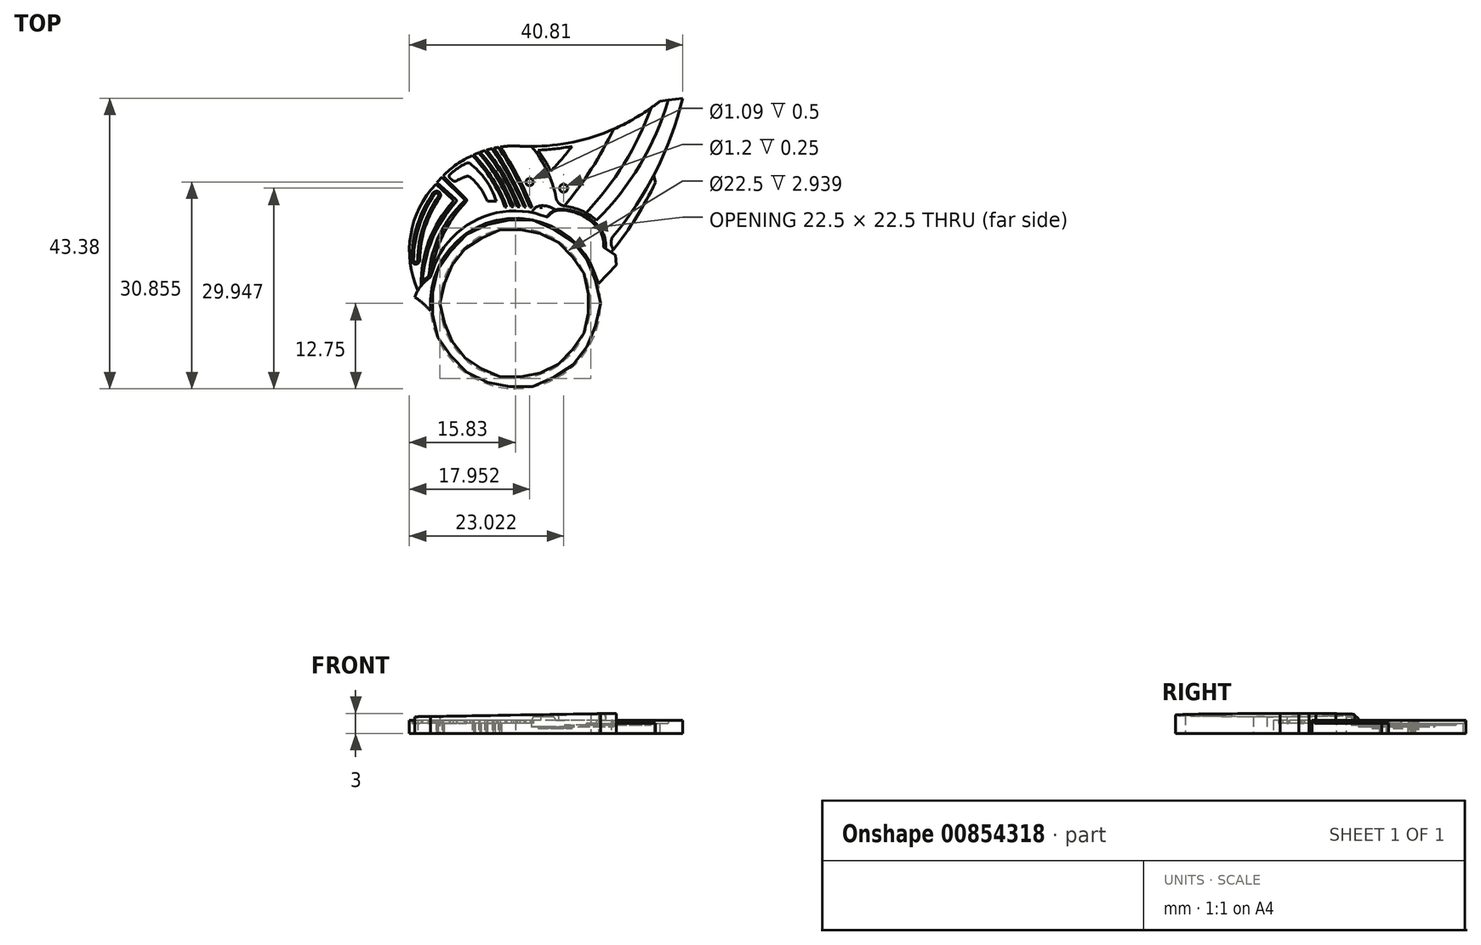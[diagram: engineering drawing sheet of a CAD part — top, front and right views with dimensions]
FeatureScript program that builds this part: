
annotation { "Feature Type Name" : "Feature", "Feature Type Description" : "" }
export const myFeature = defineFeature(function(context is Context, id is Id, definition is map)
    precondition{}
    {
        {
            var Q0;
            Q0=qCreatedBy(makeId("Top.planeOp"),FACE);
            var sketch = newSketch(context, id + "F0", { "sketchPlane" : qUnion([Q0])});
            skCircle(sketch, "E0", {"center": v(0, 0) * mm, "radius": 11.25 * mm});
            skCircle(sketch, "E1", {"center": v(0, 0) * mm, "radius": 12.75 * mm});
            skCircle(sketch, "E2", {"center": v(0, 0) * mm, "radius": 10.25 * mm});
            skSolve(sketch);
        }
        {
            var Q0;
            Q0=makeQuery(id+"F0.imprint","IMPRINT",FACE,{"disambiguationData":[TD([[makeQuery(id+"F0.imprint","IMPRINT",EDGE,{"derivedFrom":sQuery(id+"F0.wireOp",EDGE,"E0")}),-1.0]])]});
            var Q1;
            Q1=makeQuery(id+"F0.imprint","IMPRINT",FACE,{"disambiguationData":[TD([[makeQuery(id+"F0.imprint","IMPRINT",EDGE,{"derivedFrom":sQuery(id+"F0.wireOp",EDGE,"E0")}),1.0]])]});
            extrude(context, id + "F1", {"entities" : qUnion([Q0, Q1]), "endBound" : BoundingType.SYMMETRIC, "oppositeDirection" : true, "depth" : 9 * mm, "offsetDistance" : 25 * mm});
        }
        {
            var Q0;
            Q0=makeQuery(id+"F0.imprint","IMPRINT",FACE,{"disambiguationData":[TD([[makeQuery(id+"F0.imprint","IMPRINT",EDGE,{"derivedFrom":sQuery(id+"F0.wireOp",EDGE,"E0")}),1.0]])]});
            extrude(context, id + "F2", {"entities" : qUnion([Q0]), "operationType" : NewBodyOperationType.REMOVE, "depth" : 3.5 * mm, "offsetDistance" : 25 * mm});
        }
        {
            var Q0;
            Q0=qCreatedBy(makeId("Top.planeOp"),FACE);
            var sketch = newSketch(context, id + "F3", { "sketchPlane" : qUnion([Q0])});
            skCircle(sketch, "E3", {"center": v(0, 0) * mm, "radius": 10.25 * mm});
            skArc(sketch, "E4", {"start": v(-2, 8) * mm, "mid": v(-8.25, 0) * mm, "end": v(-2, -8) * mm});
            skLineSegment(sketch, "E5.left", {"start": v(-2, 8) * mm, "end": v(-2, -8) * mm});
            skLineSegment(sketch, "E5.right", {"start": v(2, 8) * mm, "end": v(2, -8) * mm});
            skLineSegment(sketch, "E6", {"start": v(-2, 8) * mm, "end": v(2, -8) * mm, "construction": true});
            skArc(sketch, "E7.trimOffspring", {"start": v(2, -8) * mm, "mid": v(8.25, 0) * mm, "end": v(2, 8) * mm});
            skSolve(sketch);
        }
        {
            var Q0;
            Q0=makeQuery(id+"F3.imprint","IMPRINT",FACE,{"disambiguationData":[TD([[makeQuery(id+"F3.imprint","IMPRINT",EDGE,{"derivedFrom":sQuery(id+"F3.wireOp",EDGE,"E3")}),1.0]])]});
            extrude(context, id + "F4", {"entities" : qUnion([Q0]), "oppositeDirection" : true, "depth" : 2 * mm, "offsetDistance" : 25 * mm});
        }
        {
            var Q0;
            Q0=makeQuery(id+"F4.opExtrude","SWEPT_BODY",BODY,{"disambiguationData":[OSD([sQuery(id+"F3.wireOp",EDGE,"E3"),sQuery(id+"F3.wireOp",EDGE,"E4"),sQuery(id+"F3.wireOp",EDGE,"E5.left"),sQuery(id+"F3.wireOp",EDGE,"E5.right"),sQuery(id+"F3.wireOp",EDGE,"E7.trimOffspring")])]});
            deleteBodies(context, id + "F5", {"entities" : qUnion([Q0])});
        }
        {
            var Q0;
            Q0=makeQuery(id+"F0.imprint","IMPRINT",FACE,{"disambiguationData":[TD([[makeQuery(id+"F0.imprint","IMPRINT",EDGE,{"derivedFrom":sQuery(id+"F0.wireOp",EDGE,"E0")}),1.0]])]});
            extrude(context, id + "F6", {"entities" : qUnion([Q0]), "operationType" : NewBodyOperationType.REMOVE, "oppositeDirection" : true, "depth" : 3.5 * mm, "offsetDistance" : 25 * mm});
        }
        {
            var Q0;
            Q0=qCreatedBy(makeId("Top.planeOp"),FACE);
            var sketch = newSketch(context, id + "F7", { "sketchPlane" : qUnion([Q0])});
            skCircle(sketch, "E8.cCircle", {"center": v(0, 0) * mm, "radius": 12.75 * mm});
            skLineSegment(sketch, "E8.0", {"start": v(-12.75, 0) * mm, "end": v(6.38, 11.04) * mm, "construction": true});
            skLineSegment(sketch, "E8.1", {"start": v(6.37, 11.04) * mm, "end": v(6.38, -11.04) * mm, "construction": true});
            skLineSegment(sketch, "E8.2", {"start": v(6.38, -11.04) * mm, "end": v(-12.75, 0) * mm, "construction": true});
            skCircle(sketch, "E9.0", {"center": v(0, 0) * mm, "radius": 12.75 * mm, "construction": true});
            skArc(sketch, "E10", {"start": v(0, 23.52) * mm, "mid": v(-1.13, 23.48) * mm, "end": v(-2.26, 23.35) * mm});
            skArc(sketch, "E11", {"start": v(0, 23.52) * mm, "mid": v(11.42, 24.82) * mm, "end": v(21.58, 30.2) * mm});
            skLineSegment(sketch, "E12", {"start": v(21.58, 30.2) * mm, "end": v(24.98, 30.63) * mm});
            skArc(sketch, "E13", {"start": v(14.56, 10) * mm, "mid": v(20.98, 19.7) * mm, "end": v(24.98, 30.63) * mm});
            skLineSegment(sketch, "E14", {"start": v(20.67, 19.1) * mm, "end": v(20.94, 18.08) * mm});
            skArc(sketch, "E15", {"start": v(14.3, 7.63) * mm, "mid": v(17.93, 12.66) * mm, "end": v(20.94, 18.08) * mm});
            skArc(sketch, "E16", {"start": v(12.1, 12.4) * mm, "mid": v(18.62, 20.7) * mm, "end": v(22.83, 30.36) * mm});
            skArc(sketch, "E17", {"start": v(10.53, 13.5) * mm, "mid": v(16.23, 20.84) * mm, "end": v(20.26, 29.2) * mm});
            skArc(sketch, "E18", {"start": v(7.32, 14.55) * mm, "mid": v(11.36, 20.06) * mm, "end": v(14.68, 26.03) * mm});
            skArc(sketch, "E19", {"start": v(6.08, 15.72) * mm, "mid": v(4.73, 19.82) * mm, "end": v(2.38, 23.43) * mm});
            skArc(sketch, "E20", {"start": v(12.1, 12.4) * mm, "mid": v(9.87, 13.84) * mm, "end": v(7.32, 14.55) * mm});
            skArc(sketch, "E21", {"start": v(6.08, 15.72) * mm, "mid": v(6.51, 14.94) * mm, "end": v(7.32, 14.55) * mm});
            skArc(sketch, "E22", {"start": v(5.26, 19.75) * mm, "mid": v(4.42, 21.36) * mm, "end": v(3.4, 22.88) * mm});
            skArc(sketch, "E23", {"start": v(3.4, 22.88) * mm, "mid": v(5.94, 23.07) * mm, "end": v(8.44, 23.46) * mm});
            skArc(sketch, "E24", {"start": v(5.26, 19.75) * mm, "mid": v(6.92, 21.55) * mm, "end": v(8.44, 23.46) * mm});
            skArc(sketch, "E25", {"start": v(2.48, 14.32) * mm, "mid": v(0.36, 18.97) * mm, "end": v(-2.26, 23.35) * mm});
            skArc(sketch, "E26", {"start": v(2.17, 14.35) * mm, "mid": v(0.05, 18.95) * mm, "end": v(-2.56, 23.3) * mm});
            skLineSegment(sketch, "E27", {"start": v(2.48, 14.32) * mm, "end": v(2.17, 14.35) * mm});
            skArc(sketch, "E28", {"start": v(-2.85, 15.27) * mm, "mid": v(-4.42, 18.41) * mm, "end": v(-6.85, 20.94) * mm});
            skArc(sketch, "E29", {"start": v(-7.36, 20.9) * mm, "mid": v(-8.63, 20.16) * mm, "end": v(-9.78, 19.23) * mm});
            skArc(sketch, "E30", {"start": v(-7.32, 18.95) * mm, "mid": v(-8.06, 18.68) * mm, "end": v(-8.75, 18.32) * mm});
            skArc(sketch, "E31", {"start": v(-4.18, 15.24) * mm, "mid": v(-5.24, 17.21) * mm, "end": v(-6.78, 18.84) * mm});
            skArc(sketch, "E32", {"start": v(-6.78, 18.84) * mm, "mid": v(-7.04, 18.97) * mm, "end": v(-7.32, 18.95) * mm});
            skArc(sketch, "E33", {"start": v(-6.85, 20.94) * mm, "mid": v(-7.1, 20.98) * mm, "end": v(-7.36, 20.9) * mm});
            skLineSegment(sketch, "E34", {"start": v(-9.8, 18.74) * mm, "end": v(-9.36, 18.33) * mm});
            skLineSegment(sketch, "E35", {"start": v(-4.18, 15.24) * mm, "end": v(-2.85, 15.27) * mm});
            skArc(sketch, "E36", {"start": v(-9.78, 19.23) * mm, "mid": v(-9.9, 19) * mm, "end": v(-9.8, 18.74) * mm});
            skArc(sketch, "E37", {"start": v(-9.36, 18.33) * mm, "mid": v(-9.06, 18.21) * mm, "end": v(-8.75, 18.32) * mm});
            skCircle(sketch, "E38", {"center": v(7.2, 17.2) * mm, "radius": 0.6 * mm});
            skCircle(sketch, "E39", {"center": v(2.12, 18.1) * mm, "radius": 0.55 * mm});
            skLineSegment(sketch, "E40", {"start": v(-10.8, 19.02) * mm, "end": v(-7.38, 15.63) * mm});
            skLineSegment(sketch, "E41", {"start": v(-10.8, 19.02) * mm, "end": v(-6.53, 23.33) * mm, "construction": true});
            skLineSegment(sketch, "E42", {"start": v(-10.98, 18.83) * mm, "end": v(-7.67, 15.55) * mm});
            skArc(sketch, "E43", {"start": v(-12.7, -1.1) * mm, "mid": v(-13.79, 0) * mm, "end": v(-15.02, 0.93) * mm});
            skArc(sketch, "E44", {"start": v(-12.67, 3.93) * mm, "mid": v(-14.09, 2.62) * mm, "end": v(-15.02, 0.93) * mm});
            skArc(sketch, "E45", {"start": v(4.7, 12.9) * mm, "mid": v(-6.04, 12.38) * mm, "end": v(-12.67, 3.93) * mm});
            skArc(sketch, "E46", {"start": v(14.56, 10) * mm, "mid": v(14.31, 9) * mm, "end": v(14.6, 8) * mm});
            skArc(sketch, "E47", {"start": v(12.67, 11.21) * mm, "mid": v(9.9, 13.36) * mm, "end": v(6.47, 14.07) * mm});
            skArc(sketch, "E48", {"start": v(13.44, 8.22) * mm, "mid": v(13.34, 9.8) * mm, "end": v(12.67, 11.21) * mm});
            skArc(sketch, "E49", {"start": v(6.47, 14.07) * mm, "mid": v(5.47, 13.66) * mm, "end": v(4.7, 12.9) * mm});
            skLineSegment(sketch, "E50", {"start": v(13.44, 8.22) * mm, "end": v(14.92, 7.21) * mm});
            skLineSegment(sketch, "E51", {"start": v(14.92, 7.21) * mm, "end": v(15.05, 5.7) * mm});
            skLineSegment(sketch, "E52", {"start": v(15.05, 5.7) * mm, "end": v(12.41, 2.9) * mm});
            skArc(sketch, "E53", {"start": v(-7.63, 15.26) * mm, "mid": v(-11.33, 10.22) * mm, "end": v(-12.9, 4.17) * mm});
            skArc(sketch, "E54", {"start": v(-7.34, 15.17) * mm, "mid": v(-10.84, 10.16) * mm, "end": v(-12.58, 4.3) * mm});
            skArc(sketch, "E55", {"start": v(-13.08, 3.93) * mm, "mid": v(-13.5, 3.62) * mm, "end": v(-13.86, 3.26) * mm});
            skArc(sketch, "E56", {"start": v(-8.9, 15.08) * mm, "mid": v(-12.4, 9.6) * mm, "end": v(-13.86, 3.26) * mm});
            skArc(sketch, "E57", {"start": v(-11.88, 17.81) * mm, "mid": v(-15.62, 10.26) * mm, "end": v(-14.58, 1.89) * mm});
            skLineSegment(sketch, "E58", {"start": v(-11.88, 17.81) * mm, "end": v(-9.33, 15.47) * mm});
            skLineSegment(sketch, "E59", {"start": v(-8.93, 15.6) * mm, "end": v(-11.7, 18.04) * mm});
            skArc(sketch, "E60", {"start": v(-9.38, 15.14) * mm, "mid": v(-12.9, 9.32) * mm, "end": v(-14.09, 2.62) * mm});
            skArc(sketch, "E61", {"start": v(-13.08, 3.93) * mm, "mid": v(-12.96, 4.03) * mm, "end": v(-12.9, 4.17) * mm});
            skArc(sketch, "E62", {"start": v(-9.38, 15.14) * mm, "mid": v(-9.3, 15.3) * mm, "end": v(-9.33, 15.47) * mm});
            skArc(sketch, "E63", {"start": v(-8.9, 15.08) * mm, "mid": v(-8.8, 15.34) * mm, "end": v(-8.93, 15.6) * mm});
            skArc(sketch, "E64", {"start": v(-7.63, 15.26) * mm, "mid": v(-7.6, 15.41) * mm, "end": v(-7.67, 15.55) * mm});
            skArc(sketch, "E65", {"start": v(-7.34, 15.17) * mm, "mid": v(-7.28, 15.4) * mm, "end": v(-7.38, 15.63) * mm});
            skArc(sketch, "E66", {"start": v(-11.5, 16) * mm, "mid": v(-13.77, 11.46) * mm, "end": v(-14.58, 6.46) * mm});
            skArc(sketch, "E67", {"start": v(-12.02, 16.34) * mm, "mid": v(-14.35, 11.64) * mm, "end": v(-15.2, 6.47) * mm});
            skArc(sketch, "E68", {"start": v(-15.2, 6.47) * mm, "mid": v(-14.9, 6.15) * mm, "end": v(-14.58, 6.46) * mm});
            skArc(sketch, "E69", {"start": v(-11.5, 16) * mm, "mid": v(-11.6, 16.4) * mm, "end": v(-12.02, 16.34) * mm});
            skArc(sketch, "E70.0", {"start": v(-11.24, 15.83) * mm, "mid": v(-13.48, 11.38) * mm, "end": v(-14.28, 6.46) * mm});
            skArc(sketch, "E70.1", {"start": v(-11.24, 15.83) * mm, "mid": v(-11.43, 16.66) * mm, "end": v(-12.27, 16.51) * mm});
            skArc(sketch, "E70.2", {"start": v(-12.27, 16.51) * mm, "mid": v(-14.63, 11.74) * mm, "end": v(-15.5, 6.48) * mm});
            skArc(sketch, "E70.3", {"start": v(-15.5, 6.48) * mm, "mid": v(-14.9, 5.85) * mm, "end": v(-14.28, 6.46) * mm});
            skArc(sketch, "E71", {"start": v(5.99, 13.93) * mm, "mid": v(4.96, 14.45) * mm, "end": v(3.82, 14.58) * mm});
            skArc(sketch, "E72", {"start": v(3.82, 14.58) * mm, "mid": v(3, 14.28) * mm, "end": v(2.47, 13.57) * mm});
            skLineSegment(sketch, "E73", {"start": v(-11.76, 17.7) * mm, "end": v(-11.56, 17.92) * mm});
            skLineSegment(sketch, "E74", {"start": v(-10.84, 18.69) * mm, "end": v(-10.66, 18.87) * mm});
            skLineSegment(sketch, "E75", {"start": v(-2.4, 23.05) * mm, "end": v(-2.1, 23.1) * mm});
            skArc(sketch, "E76", {"start": v(2.17, 14.35) * mm, "mid": v(0.32, 14.41) * mm, "end": v(-1.53, 14.35) * mm});
            skArc(sketch, "E77", {"start": v(-1.53, 14.35) * mm, "mid": v(-3.6, 18.46) * mm, "end": v(-6.43, 22.1) * mm});
            skArc(sketch, "E78", {"start": v(-1.28, 14.36) * mm, "mid": v(-3.34, 18.53) * mm, "end": v(-6.19, 22.2) * mm});
            skArc(sketch, "E79", {"start": v(1.53, 14.38) * mm, "mid": v(-0.62, 18.9) * mm, "end": v(-3.2, 23.18) * mm});
            skArc(sketch, "E80", {"start": v(1.28, 14.4) * mm, "mid": v(-0.9, 18.87) * mm, "end": v(-3.5, 23.11) * mm});
            skArc(sketch, "E81", {"start": v(0.64, 14.41) * mm, "mid": v(-1.5, 18.85) * mm, "end": v(-4.3, 22.9) * mm});
            skArc(sketch, "E82", {"start": v(0.26, 14.41) * mm, "mid": v(-1.79, 18.83) * mm, "end": v(-4.6, 22.8) * mm});
            skArc(sketch, "E83", {"start": v(-0.3, 14.4) * mm, "mid": v(-2.38, 18.74) * mm, "end": v(-5.28, 22.57) * mm});
            skArc(sketch, "E84", {"start": v(-0.62, 14.4) * mm, "mid": v(-2.7, 18.66) * mm, "end": v(-5.5, 22.5) * mm});
            skArc(sketch, "E85", {"start": v(-3.04, 22.95) * mm, "mid": v(-3.2, 22.92) * mm, "end": v(-3.34, 22.89) * mm});
            skArc(sketch, "E86.trimOffspring", {"start": v(-4.14, 22.7) * mm, "mid": v(-4.28, 22.65) * mm, "end": v(-4.43, 22.61) * mm});
            skArc(sketch, "E87.trimOffspring", {"start": v(-5.1, 22.39) * mm, "mid": v(-5.22, 22.35) * mm, "end": v(-5.34, 22.3) * mm});
            skArc(sketch, "E88.trimOffspring", {"start": v(-6.02, 22.03) * mm, "mid": v(-6.14, 21.97) * mm, "end": v(-6.26, 21.92) * mm});
            skArc(sketch, "E89.trimOffspring", {"start": v(-6.43, 22.1) * mm, "mid": v(-8.75, 20.75) * mm, "end": v(-10.8, 19.02) * mm});
            skArc(sketch, "E90.trimOffspring", {"start": v(-5.5, 22.5) * mm, "mid": v(-5.85, 22.35) * mm, "end": v(-6.19, 22.2) * mm});
            skArc(sketch, "E91.trimOffspring", {"start": v(-4.6, 22.8) * mm, "mid": v(-4.94, 22.7) * mm, "end": v(-5.28, 22.57) * mm});
            skArc(sketch, "E92.trimOffspring", {"start": v(-3.5, 23.11) * mm, "mid": v(-3.9, 23.01) * mm, "end": v(-4.3, 22.9) * mm});
            skArc(sketch, "E93.trimOffspring", {"start": v(-2.56, 23.3) * mm, "mid": v(-2.88, 23.24) * mm, "end": v(-3.2, 23.18) * mm});
            skArc(sketch, "E94.trimOffspring", {"start": v(-10.98, 18.83) * mm, "mid": v(-11.35, 18.44) * mm, "end": v(-11.7, 18.04) * mm});
            skSolve(sketch);
        }
        {
            var Q0;
            {var subQ8=sQuery(id+"F7.wireOp",EDGE,"E43");Q0=makeQuery(id+"F7.imprint","IMPRINT",FACE,{"disambiguationData":[TD([[makeQuery(id+"F7.imprint","IMPRINT",EDGE,{"derivedFrom":subQ8}),-1.0]])]});}
            extrude(context, id + "F8", {"entities" : qUnion([Q0]), "endBound" : BoundingType.SYMMETRIC, "depth" : 6 * mm, "offsetDistance" : 25 * mm});
        }
        {
            var Q0;
            {var subQ9=sQuery(id+"F7.wireOp",EDGE,"E16");Q0=makeQuery(id+"F7.imprint","IMPRINT",FACE,{"disambiguationData":[TD([[makeQuery(id+"F7.imprint","IMPRINT",EDGE,{"derivedFrom":subQ9}),-1.0]])]});}
            var Q1;
            {var subQ1=sQuery(id+"F7.wireOp",EDGE,"E57");Q1=makeQuery(id+"F7.imprint","IMPRINT",FACE,{"disambiguationData":[TD([[makeQuery(id+"F7.imprint","IMPRINT",EDGE,{"derivedFrom":subQ1}),1.0]])]});}
            var Q2;
            Q2=makeQuery(id+"F7.imprint","IMPRINT",FACE,{"disambiguationData":[TD([[makeQuery(id+"F7.imprint","IMPRINT",EDGE,{"derivedFrom":sQuery(id+"F7.wireOp",EDGE,"E66")}),-1.0]])]});
            var Q3;
            {var subQ0=sQuery(id+"F7.wireOp",EDGE,"E42");Q3=makeQuery(id+"F7.imprint","IMPRINT",FACE,{"disambiguationData":[TD([[makeQuery(id+"F7.imprint","IMPRINT",EDGE,{"derivedFrom":subQ0}),-1.0]])]});}
            var Q4;
            {var subQ5=sQuery(id+"F7.wireOp",EDGE,"E93.trimOffspring");Q4=makeQuery(id+"F7.imprint","IMPRINT",FACE,{"disambiguationData":[TD([[makeQuery(id+"F7.imprint","IMPRINT",EDGE,{"derivedFrom":subQ5}),1.0]])]});}
            var Q5;
            {var subQ4=sQuery(id+"F7.wireOp",EDGE,"E92.trimOffspring");Q5=makeQuery(id+"F7.imprint","IMPRINT",FACE,{"disambiguationData":[TD([[makeQuery(id+"F7.imprint","IMPRINT",EDGE,{"derivedFrom":subQ4}),1.0]])]});}
            var Q6;
            {var subQ7=sQuery(id+"F7.wireOp",EDGE,"E91.trimOffspring");Q6=makeQuery(id+"F7.imprint","IMPRINT",FACE,{"disambiguationData":[TD([[makeQuery(id+"F7.imprint","IMPRINT",EDGE,{"derivedFrom":subQ7}),1.0]])]});}
            var Q7;
            {var subQ4=sQuery(id+"F7.wireOp",EDGE,"E90.trimOffspring");Q7=makeQuery(id+"F7.imprint","IMPRINT",FACE,{"disambiguationData":[TD([[makeQuery(id+"F7.imprint","IMPRINT",EDGE,{"derivedFrom":subQ4}),1.0]])]});}
            extrude(context, id + "F9", {"entities" : qUnion([Q0, Q1, Q2, Q3, Q4, Q5, Q6, Q7]), "operationType" : NewBodyOperationType.ADD, "endBound" : BoundingType.SYMMETRIC, "depth" : 4 * mm, "offsetDistance" : 25 * mm});
        }
        {
            var Q0;
            {var subQ4=sQuery(id+"F7.wireOp",EDGE,"E71");Q0=makeQuery(id+"F7.imprint","IMPRINT",FACE,{"disambiguationData":[TD([[makeQuery(id+"F7.imprint","IMPRINT",EDGE,{"derivedFrom":subQ4}),1.0]])]});}
            extrude(context, id + "F10", {"entities" : qUnion([Q0]), "operationType" : NewBodyOperationType.ADD, "endBound" : BoundingType.SYMMETRIC, "depth" : 5 * mm, "offsetDistance" : 25 * mm});
        }
        {
            var Q0;
            Q0=makeQuery(id+"F7.imprint","IMPRINT",FACE,{"disambiguationData":[TD([[makeQuery(id+"F7.imprint","IMPRINT",EDGE,{"derivedFrom":sQuery(id+"F7.wireOp",EDGE,"E28")}),1.0]])]});
            var Q1;
            {var subQ5=sQuery(id+"F7.wireOp",EDGE,"E40");Q1=makeQuery(id+"F7.imprint","IMPRINT",FACE,{"disambiguationData":[TD([[makeQuery(id+"F7.imprint","IMPRINT",EDGE,{"derivedFrom":subQ5}),-1.0]])]});}
            var Q2;
            Q2=makeQuery(id+"F7.imprint","IMPRINT",FACE,{"disambiguationData":[TD([[makeQuery(id+"F7.imprint","IMPRINT",EDGE,{"derivedFrom":sQuery(id+"F7.wireOp",EDGE,"E66")}),1.0]])]});
            var Q3;
            Q3=makeQuery(id+"F7.imprint","IMPRINT",FACE,{"disambiguationData":[TD([[makeQuery(id+"F7.imprint","IMPRINT",EDGE,{"derivedFrom":sQuery(id+"F7.wireOp",EDGE,"E39")}),1.0]])]});
            var Q4;
            {var subQ2=sQuery(id+"F7.wireOp",EDGE,"E14");Q4=makeQuery(id+"F7.imprint","IMPRINT",FACE,{"disambiguationData":[TD([[makeQuery(id+"F7.imprint","IMPRINT",EDGE,{"derivedFrom":subQ2}),-1.0]])]});}
            var Q5;
            {var subQ5=sQuery(id+"F7.wireOp",EDGE,"E88.trimOffspring");Q5=makeQuery(id+"F7.imprint","IMPRINT",FACE,{"disambiguationData":[TD([[makeQuery(id+"F7.imprint","IMPRINT",EDGE,{"derivedFrom":subQ5}),1.0]])]});}
            var Q6;
            {var subQ5=sQuery(id+"F7.wireOp",EDGE,"E87.trimOffspring");Q6=makeQuery(id+"F7.imprint","IMPRINT",FACE,{"disambiguationData":[TD([[makeQuery(id+"F7.imprint","IMPRINT",EDGE,{"derivedFrom":subQ5}),1.0]])]});}
            var Q7;
            {var subQ5=sQuery(id+"F7.wireOp",EDGE,"E86.trimOffspring");Q7=makeQuery(id+"F7.imprint","IMPRINT",FACE,{"disambiguationData":[TD([[makeQuery(id+"F7.imprint","IMPRINT",EDGE,{"derivedFrom":subQ5}),1.0]])]});}
            var Q8;
            {var subQ5=sQuery(id+"F7.wireOp",EDGE,"E85");Q8=makeQuery(id+"F7.imprint","IMPRINT",FACE,{"disambiguationData":[TD([[makeQuery(id+"F7.imprint","IMPRINT",EDGE,{"derivedFrom":subQ5}),1.0]])]});}
            var Q9;
            {var subQ0=sQuery(id+"F7.wireOp",EDGE,"E27");Q9=makeQuery(id+"F7.imprint","IMPRINT",FACE,{"disambiguationData":[TD([[makeQuery(id+"F7.imprint","IMPRINT",EDGE,{"derivedFrom":subQ0}),-1.0]])]});}
            var Q10;
            {var subQ1=sQuery(id+"F7.wireOp",EDGE,"E16");Q10=makeQuery(id+"F7.imprint","IMPRINT",FACE,{"disambiguationData":[TD([[makeQuery(id+"F7.imprint","IMPRINT",EDGE,{"derivedFrom":subQ1}),1.0]])]});}
            extrude(context, id + "F11", {"entities" : qUnion([Q0, Q1, Q2, Q3, Q4, Q5, Q6, Q7, Q8, Q9, Q10]), "operationType" : NewBodyOperationType.ADD, "endBound" : BoundingType.SYMMETRIC, "depth" : 3 * mm, "offsetDistance" : 25 * mm});
        }
        {
            var Q0;
            {var subQ0=sQuery(id+"F7.wireOp",EDGE,"E17");Q0=makeQuery(id+"F7.imprint","IMPRINT",FACE,{"disambiguationData":[TD([[makeQuery(id+"F7.imprint","IMPRINT",EDGE,{"derivedFrom":subQ0}),1.0]])]});}
            extrude(context, id + "F12", {"entities" : qUnion([Q0]), "operationType" : NewBodyOperationType.ADD, "endBound" : BoundingType.SYMMETRIC, "depth" : 2.5 * mm, "offsetDistance" : 25 * mm});
        }
        {
            var Q0;
            {var subQ1=sQuery(id+"F7.wireOp",EDGE,"E18");Q0=makeQuery(id+"F7.imprint","IMPRINT",FACE,{"disambiguationData":[TD([[makeQuery(id+"F7.imprint","IMPRINT",EDGE,{"derivedFrom":subQ1}),1.0]])]});}
            extrude(context, id + "F13", {"entities" : qUnion([Q0]), "operationType" : NewBodyOperationType.ADD, "endBound" : BoundingType.SYMMETRIC, "depth" : 2 * mm, "offsetDistance" : 25 * mm});
        }
        {
            var Q0;
            Q0=makeQuery(id+"F7.imprint","IMPRINT",FACE,{"disambiguationData":[TD([[makeQuery(id+"F7.imprint","IMPRINT",EDGE,{"derivedFrom":sQuery(id+"F7.wireOp",EDGE,"E38")}),1.0]])]});
            var Q1;
            Q1=makeQuery(id+"F7.imprint","IMPRINT",FACE,{"disambiguationData":[TD([[makeQuery(id+"F7.imprint","IMPRINT",EDGE,{"derivedFrom":sQuery(id+"F7.wireOp",EDGE,"E22")}),-1.0]])]});
            extrude(context, id + "F14", {"entities" : qUnion([Q0, Q1]), "operationType" : NewBodyOperationType.ADD, "endBound" : BoundingType.SYMMETRIC, "depth" : 1.5 * mm, "offsetDistance" : 25 * mm});
        }
        {
            var Q0;
            Q0=makeQuery(id+"F8.opExtrude","CAP_EDGE",EDGE,{"disambiguationData":[OSD([sQuery(id+"F7.wireOp",EDGE,"E49")])],"isStart":false});
            var Q1;
            Q1=makeQuery(id+"F8.opExtrude","CAP_EDGE",EDGE,{"disambiguationData":[OSD([sQuery(id+"F7.wireOp",EDGE,"E47")])],"isStart":false});
            var Q2;
            Q2=makeQuery(id+"F8.opExtrude","CAP_EDGE",EDGE,{"disambiguationData":[OSD([sQuery(id+"F7.wireOp",EDGE,"E48")])],"isStart":false});
            var Q3;
            Q3=makeQuery(id+"F10.opExtrude","CAP_EDGE",EDGE,{"disambiguationData":[OSD([sQuery(id+"F7.wireOp",EDGE,"E71")])],"isStart":false});
            var Q4;
            Q4=makeQuery(id+"F10.opExtrude","CAP_EDGE",EDGE,{"disambiguationData":[OSD([sQuery(id+"F7.wireOp",EDGE,"E72")])],"isStart":false});
            var Q5;
            Q5=makeQuery(id+"F10.opExtrude","CAP_EDGE",EDGE,{"disambiguationData":[OSD([sQuery(id+"F7.wireOp",EDGE,"E72")])],"isStart":true});
            var Q6;
            Q6=makeQuery(id+"F10.opExtrude","CAP_EDGE",EDGE,{"disambiguationData":[OSD([sQuery(id+"F7.wireOp",EDGE,"E71")])],"isStart":true});
            var Q7;
            Q7=makeQuery(id+"F8.opExtrude","CAP_EDGE",EDGE,{"disambiguationData":[OSD([sQuery(id+"F7.wireOp",EDGE,"E49")])],"isStart":true});
            var Q8;
            Q8=makeQuery(id+"F8.opExtrude","CAP_EDGE",EDGE,{"disambiguationData":[OSD([sQuery(id+"F7.wireOp",EDGE,"E47")])],"isStart":true});
            var Q9;
            Q9=makeQuery(id+"F8.opExtrude","CAP_EDGE",EDGE,{"disambiguationData":[OSD([sQuery(id+"F7.wireOp",EDGE,"E48")])],"isStart":true});
            fillet(context, id + "F15", {"entities" : qUnion([Q0, Q1, Q2, Q3, Q4, Q5, Q6, Q7, Q8, Q9]), "radius" : .45 * mm, "tangentPropagation" : true, "allowEdgeOverflow" : false});
        }
        {
            var Q0;
            Q0=qCreatedBy(makeId("Front.planeOp"),FACE);
            var sketch = newSketch(context, id + "F16", { "sketchPlane" : qUnion([Q0])});
            skLineSegment(sketch, "E95.0", {"start": v(-12.75, 4.5) * mm, "end": v(12.75, 4.5) * mm, "construction": true});
            skLineSegment(sketch, "E96", {"start": v(-15.02, 2.5) * mm, "end": v(15.05, 3) * mm});
            skLineSegment(sketch, "E97.0", {"start": v(15.05, 3) * mm, "end": v(15.05, -3) * mm, "construction": true});
            skLineSegment(sketch, "E98", {"start": v(15.05, 3) * mm, "end": v(18.67, 3) * mm});
            skLineSegment(sketch, "E99", {"start": v(18.67, 3) * mm, "end": v(15.55, 6.61) * mm});
            skLineSegment(sketch, "E100", {"start": v(15.55, 6.61) * mm, "end": v(-16.77, 6.35) * mm});
            skLineSegment(sketch, "E101", {"start": v(-16.77, 6.35) * mm, "end": v(-15.02, 2.5) * mm});
            skLineSegment(sketch, "E102.0.0", {"start": v(5.53, 2.5) * mm, "end": v(3.85, 2.5) * mm, "construction": true});
            skLineSegment(sketch, "E102.0.1", {"start": v(3.85, 2.5) * mm, "end": v(2.92, 2.5) * mm, "construction": true});
            skLineSegment(sketch, "E102.0.2", {"start": v(2.92, 2.5) * mm, "end": v(4.7, 2.5) * mm, "construction": true});
            skLineSegment(sketch, "E102.0.3", {"start": v(4.7, 2.5) * mm, "end": v(5.53, 2.5) * mm, "construction": true});
            skPoint(sketch, "E103.0", {"position": v(21.58, 0) * mm});
            skPoint(sketch, "E104.0", {"position": v(0, 0) * mm});
            skLineSegment(sketch, "E105", {"start": v(21.58, 0) * mm, "end": v(0, 0) * mm, "construction": true});
            skLineSegment(sketch, "E106.MirrorCS", {"start": v(18.67, -3) * mm, "end": v(15.55, -6.61) * mm});
            skLineSegment(sketch, "E107.MirrorCS", {"start": v(15.05, -3) * mm, "end": v(18.67, -3) * mm});
            skLineSegment(sketch, "E108.MirrorCS", {"start": v(-15.02, -2.5) * mm, "end": v(15.05, -3) * mm});
            skLineSegment(sketch, "E109.MirrorCS", {"start": v(15.55, -6.61) * mm, "end": v(-16.77, -6.35) * mm});
            skLineSegment(sketch, "E110.MirrorCS", {"start": v(-16.77, -6.35) * mm, "end": v(-15.02, -2.5) * mm});
            skSolve(sketch);
        }
        {
            var Q0;
            Q0=makeQuery(id+"F16.imprint","IMPRINT",FACE,{"disambiguationData":[TD([[makeQuery(id+"F16.imprint","IMPRINT",EDGE,{"derivedFrom":sQuery(id+"F16.wireOp",EDGE,"E96")}),1.0]])]});
            var Q1;
            Q1=makeQuery(id+"F16.imprint","IMPRINT",FACE,{"disambiguationData":[TD([[makeQuery(id+"F16.imprint","IMPRINT",EDGE,{"derivedFrom":sQuery(id+"F16.wireOp",EDGE,"E106.MirrorCS")}),-1.0]])]});
            extrude(context, id + "F17", {"entities" : qUnion([Q0, Q1]), "operationType" : NewBodyOperationType.REMOVE, "endBound" : BoundingType.SYMMETRIC, "oppositeDirection" : true, "depth" : 50 * mm, "offsetDistance" : 25 * mm});
        }
        {
            var Q0;
            Q0=qCreatedBy(makeId("Top.planeOp"),FACE);
            var sketch = newSketch(context, id + "F18", { "sketchPlane" : qUnion([Q0])});
            skCircle(sketch, "E111", {"center": v(0.27, -0.13) * mm, "radius": 68.66 * mm});
            skSolve(sketch);
        }
        {
            var Q0;
            Q0=makeQuery(id+"F18.imprint","IMPRINT",FACE,{"disambiguationData":[TD([[makeQuery(id+"F18.imprint","IMPRINT",EDGE,{"derivedFrom":sQuery(id+"F18.wireOp",EDGE,"E111")}),1.0]])]});
            extrude(context, id + "F19", {"entities" : qUnion([Q0]), "operationType" : NewBodyOperationType.REMOVE, "oppositeDirection" : true, "depth" : 25 * mm, "offsetDistance" : 25 * mm});
        }
    });
